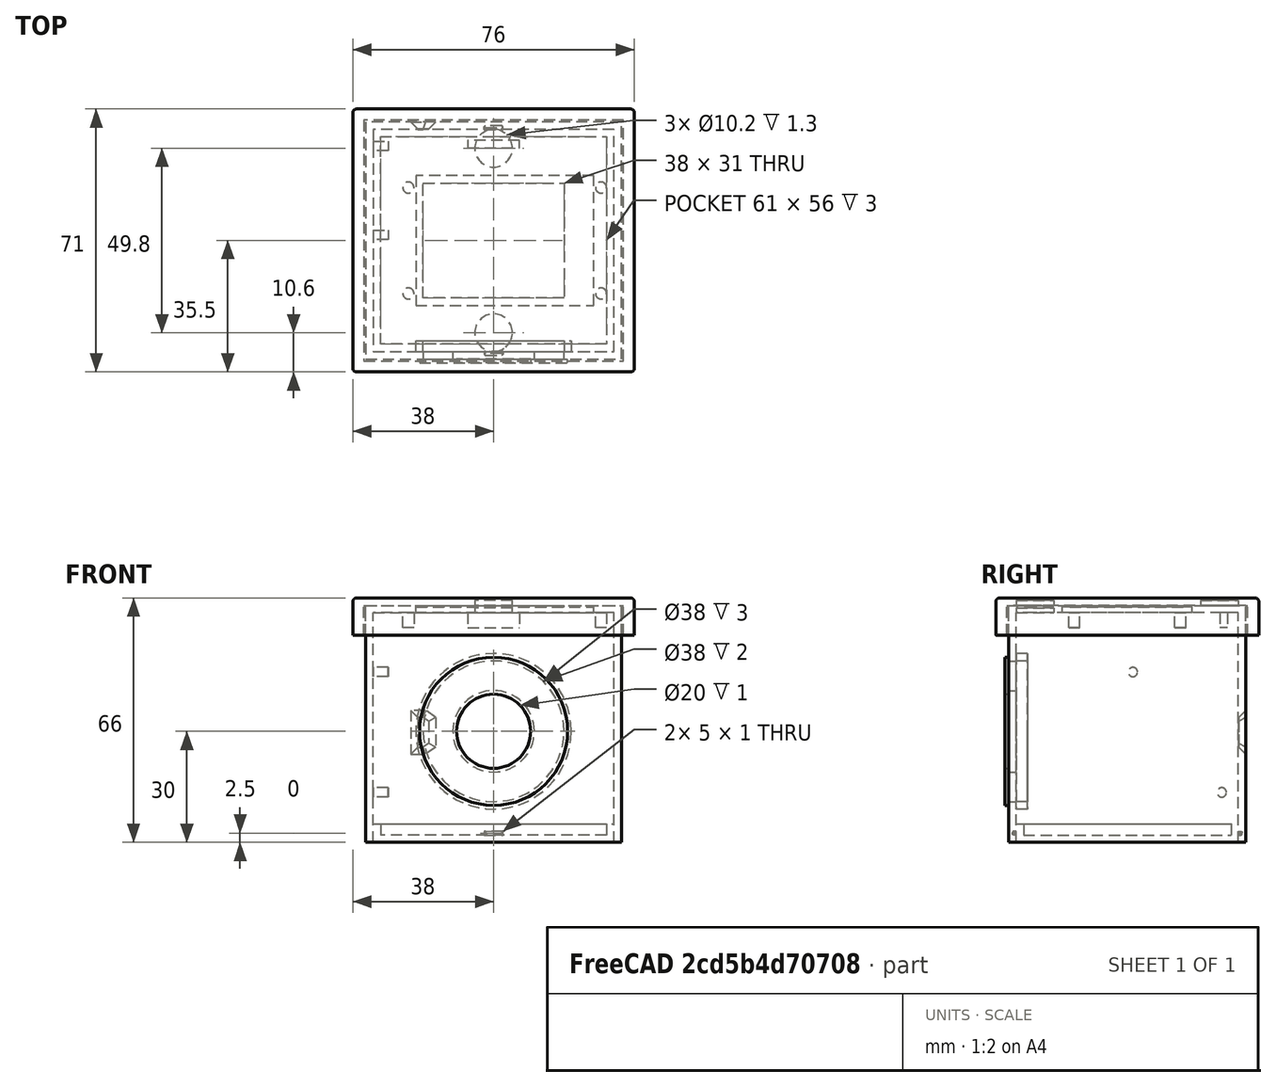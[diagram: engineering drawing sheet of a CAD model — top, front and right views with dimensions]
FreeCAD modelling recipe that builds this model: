
FCSTD DOCUMENT  (FreeCAD 0.18R16146 (Git))
Label: MessageBox
License: All rights reserved
LicenseURL: http://en.wikipedia.org/wiki/All_rights_reserved
objects: Sketcher::SketchObject×24, Part::Extrusion×24, PartDesign::ShapeBinder×17, Part::Cut×13, Part::MultiFuse×8, TechDraw::DrawViewDimension×5, TechDraw::DrawProjGroupItem×4, Part::Fillet×3, PartDesign::Body×3, TechDraw::DrawSVGTemplate×3, TechDraw::DrawPage×3, TechDraw::DrawViewSection×2, TechDraw::DrawProjGroup×2, PartDesign::Line×1, PartDesign::Plane×1, Part::Chamfer×1, Drawing::FeaturePage×1, TechDraw::DrawViewPart×1
note: 95 computed .brp shape members not serialized (recipe doc carries the construction recipe); baked Part::Feature solids carry a one-line shape summary decoded from their .brp

FEATURE [Sketcher::SketchObject] Sketch  label="Box Outline"
  MapMode = 5
  Support = -> [XY_Plane]
  sketch-geometry (6):
    g0: LineSegment StartX=-34.5 StartY=-32 StartZ=0 EndX=34.5 EndY=-32 EndZ=0
    g1: LineSegment StartX=34.5 StartY=-32 StartZ=0 EndX=34.5 EndY=32 EndZ=0
    g2: LineSegment StartX=34.5 StartY=32 StartZ=0 EndX=-34.5 EndY=32 EndZ=0
    g3: LineSegment StartX=-34.5 StartY=32 StartZ=0 EndX=-34.5 EndY=-32 EndZ=0
    g4: LineSegment [constr] StartX=-34.5 StartY=32 StartZ=0 EndX=0 EndY=0 EndZ=0
    g5: LineSegment [constr] StartX=0 StartY=0 StartZ=0 EndX=34.5 EndY=-32 EndZ=0
  constraints (17):
    c: Coincident(g0,g1)
    c: Coincident(g1,g2)
    c: Coincident(g2,g3)
    c: Coincident(g3,g0)
    c: Horizontal(g0)
    c: Horizontal(g2)
    c: Vertical(g1)
    c: Vertical(g3)
    c: DistanceX(g2,g2) = 69
    c: DistanceY(g1,g1) = 64
    c: Equal(g4,g5)
    c: Coincident(g5,g0)
    c: Coincident(g4,g-1)
    c: Coincident(g5,g-1)
    c: Equal(g5,g4)
    c: Coincident(g4,g2)
    c: Parallel(g5,g4)
FEATURE [Part::Extrusion] Extrude  label="Box Exterior Extrude"
  Base = -> Sketch
  Dir = (0,0,1)
  DirMode = 2
  FaceMakerClass = Part::FaceMakerBullseye
  LengthFwd = 64
  LengthRev = 0
  Solid = true
  Symmetric = false
FEATURE [PartDesign::ShapeBinder] CopyExtrude  label="Box Extrude"
  TraceSupport = false
FEATURE [Sketcher::SketchObject] Sketch001  label="Box Interior"
  ExternalGeometry = -> [Sketch]
  MapMode = 5
  Placement = pos=(0,0,0) rot=(1,0,0;3.14159rad)
  Support = -> [Extrude]
  sketch-geometry (4):
    g0: LineSegment StartX=32.5 StartY=-30 StartZ=0 EndX=-32.5 EndY=-30 EndZ=0
    g1: LineSegment StartX=-32.5 StartY=-30 StartZ=0 EndX=-32.5 EndY=30 EndZ=0
    g2: LineSegment StartX=-32.5 StartY=30 StartZ=0 EndX=32.5 EndY=30 EndZ=0
    g3: LineSegment StartX=32.5 StartY=30 StartZ=0 EndX=32.5 EndY=-30 EndZ=0
  constraints (12):
    c: Coincident(g0,g1)
    c: Coincident(g1,g2)
    c: Coincident(g2,g3)
    c: Coincident(g3,g0)
    c: Horizontal(g0)
    c: Horizontal(g2)
    c: Vertical(g1)
    c: Vertical(g3)
    c: DistanceY(g1,g-4) = 2
    c: DistanceY(g-6,g0) = 2
    c: DistanceX(g-4,g1) = 2
    c: DistanceX(g0,g-6) = 2
FEATURE [Part::Extrusion] Extrude001  label="Box Interior Extrude"
  Base = -> Sketch001
  Dir = (0,0,-1)
  DirMode = 2
  FaceMakerClass = Part::FaceMakerBullseye
  LengthFwd = 62
  LengthRev = 0
  Reversed = true
  Solid = true
  Symmetric = false
FEATURE [Part::Cut] Cut  label="Box Interior Cut"
  Base = -> Extrude
  Tool = -> Extrude001
FEATURE [PartDesign::ShapeBinder] CopyCut001  label="LCD Window Face"
  TraceSupport = false
FEATURE [PartDesign::ShapeBinder] CopyCut003
  TraceSupport = false
FEATURE [PartDesign::ShapeBinder] CopyCut003001
  TraceSupport = false
FEATURE [PartDesign::Line] DatumLine
  AttacherType = Attacher::AttachEngineLine
  MapMode = 29
  Placement = pos=(-0.000218501,-11.4897,2) rot=(-0.577343,0.577354,0.577354;4.18878rad)
  Support = -> [CopyCut003,CopyCut003001]
FEATURE [PartDesign::ShapeBinder] CopyCut003002
  TraceSupport = false
FEATURE [PartDesign::ShapeBinder] CopyCut003003
  TraceSupport = false
FEATURE [PartDesign::Plane] DatumPlane
  Length = 24
  MapMode = 13
  Placement = pos=(-1.67728,2.73005,1.33333) rot=(0.57735,0.57735,0.57735;2.0944rad)
  ResizeMode = 0
  Support = -> [CopyCut003002,CopyCut003003]
  Width = 24
FEATURE [PartDesign::ShapeBinder] ShapeBinder008  label="Body Interior Top"
  Placement = pos=(0,0,62) rot=(0,0,1;0rad)
  Support = -> [Cut]
  TraceSupport = false
FEATURE [Sketcher::SketchObject] Sketch002  label="LCD Window"
  ExternalGeometry = -> [ShapeBinder008]
  MapMode = 5
  Placement = pos=(0,0,62) rot=(1,0,0;3.14159rad)
  Support = -> [ShapeBinder008]
  sketch-geometry (10):
    g0: LineSegment StartX=-19 StartY=-15.5 StartZ=0 EndX=19 EndY=-15.5 EndZ=0
    g1: LineSegment StartX=19 StartY=-15.5 StartZ=0 EndX=19 EndY=15.5 EndZ=0
    g2: LineSegment StartX=19 StartY=15.5 StartZ=0 EndX=-19 EndY=15.5 EndZ=0
    g3: LineSegment [constr] StartX=19 StartY=15.5 StartZ=0 EndX=32.5 EndY=15.5 EndZ=0
    g4: LineSegment [constr] StartX=-19 StartY=15.5 StartZ=0 EndX=-32.5 EndY=15.5 EndZ=0
    g5: LineSegment [constr] StartX=-32.5 StartY=-30 StartZ=0 EndX=-32.5 EndY=7.1e-15 EndZ=0
    g6: LineSegment [constr] StartX=-32.5 StartY=5.3e-15 StartZ=0 EndX=-32.5 EndY=30 EndZ=0
    g7: LineSegment [constr] StartX=-19 StartY=15.5 StartZ=0 EndX=0 EndY=5.3e-15 EndZ=0
    g8: LineSegment [constr] StartX=0 StartY=5.3e-15 StartZ=0 EndX=19 EndY=-15.5 EndZ=0
    g9: LineSegment StartX=-19 StartY=15.5 StartZ=0 EndX=-19 EndY=-15.5 EndZ=0
  constraints (28):
    c: Coincident(g0,g1)
    c: Coincident(g1,g2)
    c: Horizontal(g0)
    c: Horizontal(g2)
    c: Vertical(g1)
    c: DistanceX(g2,g2) = 38
    c: DistanceY(g0,g2) = 31
    c: Horizontal(g3)
    c: Horizontal(g4)
    c: Equal(g3,g4)
    c: Coincident(g1,g3)
    c: Coincident(g2,g4)
    c: PointOnObject(g3,g-5)
    c: PointOnObject(g4,g-3)
    c: Equal(g5,g6)
    c: Coincident(g6,g5)
    c: Coincident(g5,g-6)
    c: Coincident(g-4,g6)
    c: Parallel(g5,g6)
    c: Coincident(g9,g2)
    c: Coincident(g9,g0)
    c: Vertical(g9)
    c: Equal(g7,g8)
    c: Coincident(g7,g2)
    c: Coincident(g7,g8)
    c: Coincident(g8,g0)
    c: Parallel(g7,g8)
    c: Horizontal(g7,g5)
FEATURE [Part::Extrusion] Extrude002  label="LCD Window Extrude"
  Base = -> Sketch002
  Dir = (0,0,-1)
  DirMode = 2
  FaceMakerClass = Part::FaceMakerBullseye
  LengthFwd = 2
  LengthRev = 0
  Reversed = true
  Solid = true
  Symmetric = false
FEATURE [Part::Cut] Cut001  label="LCD Window Cut"
  Base = -> Cut
  Tool = -> Extrude002
FEATURE [Sketcher::SketchObject] Sketch003  label="LCD Cutout"
  ExternalGeometry = -> [CopyCut001,Sketch002,ShapeBinder008]
  MapMode = 5
  Placement = pos=(0,0,62) rot=(1,0,0;3.14159rad)
  Support = -> [ShapeBinder008]
  sketch-geometry (4):
    g0: LineSegment StartX=-21 StartY=17.5 StartZ=0 EndX=27 EndY=17.5 EndZ=0
    g1: LineSegment StartX=27 StartY=17.5 StartZ=0 EndX=27 EndY=-17.5 EndZ=0
    g2: LineSegment StartX=27 StartY=-17.5 StartZ=0 EndX=-21 EndY=-17.5 EndZ=0
    g3: LineSegment StartX=-21 StartY=-17.5 StartZ=0 EndX=-21 EndY=17.5 EndZ=0
  constraints (12):
    c: Coincident(g0,g1)
    c: Coincident(g1,g2)
    c: Coincident(g2,g3)
    c: Coincident(g3,g0)
    c: Horizontal(g0)
    c: Horizontal(g2)
    c: Vertical(g1)
    c: Vertical(g3)
    c: DistanceY(g-5,g0) = 2
    c: DistanceY(g1,g-7) = 2
    c: DistanceX(g-7,g1) = 8
    c: DistanceX(g0,g-5) = 2
FEATURE [Part::Extrusion] Extrude003  label="LCD Cutout Extrude"
  Base = -> Sketch003
  Dir = (0,0,-1)
  DirMode = 2
  FaceMakerClass = Part::FaceMakerBullseye
  LengthFwd = 1.5
  LengthRev = 0
  Reversed = true
  Solid = true
  Symmetric = false
FEATURE [Part::Cut] Cut002  label="LCD Cutout Cut"
  Base = -> Cut001
  Tool = -> Extrude003
FEATURE [Sketcher::SketchObject] Sketch004  label="LCD Mounts"
  ExternalGeometry = -> [Sketch003]
  MapMode = 5
  Placement = pos=(0,0,62) rot=(1,0,0;3.14159rad)
  Support = -> [ShapeBinder008]
  sketch-geometry (12):
    g0: Circle CenterX=29 CenterY=14.3 CenterZ=0 NormalX=0 NormalY=0 NormalZ=1 AngleXU=0 Radius=1.5
    g1: Circle CenterX=-23 CenterY=14.3 CenterZ=0 NormalX=0 NormalY=0 NormalZ=1 AngleXU=0 Radius=1.5
    g2: Circle CenterX=-23 CenterY=-14.3 CenterZ=0 NormalX=0 NormalY=0 NormalZ=1 AngleXU=0 Radius=1.5
    g3: Circle CenterX=29 CenterY=-14.3 CenterZ=0 NormalX=0 NormalY=0 NormalZ=1 AngleXU=0 Radius=1.5
    g4: LineSegment [constr] StartX=27 StartY=17.5 StartZ=0 EndX=29 EndY=17.5 EndZ=0
    g5: LineSegment [constr] StartX=27 StartY=-17.5 StartZ=0 EndX=29 EndY=-17.5 EndZ=0
    g6: LineSegment [constr] StartX=-21 StartY=-17.5 StartZ=0 EndX=-23 EndY=-17.5 EndZ=0
    g7: LineSegment [constr] StartX=-21 StartY=17.5 StartZ=0 EndX=-23 EndY=17.5 EndZ=0
    g8: LineSegment [constr] StartX=-23 StartY=17.5 StartZ=0 EndX=-23 EndY=14.3 EndZ=0
    g9: LineSegment [constr] StartX=-23 StartY=-14.3 StartZ=0 EndX=-23 EndY=-17.5 EndZ=0
    g10: LineSegment [constr] StartX=29 StartY=17.5 StartZ=0 EndX=29 EndY=14.3 EndZ=0
    g11: LineSegment [constr] StartX=29 StartY=-14.3 StartZ=0 EndX=29 EndY=-17.5 EndZ=0
  constraints (32):
    c: Radius(g1) = 1.5
    c: Horizontal(g7)
    c: Horizontal(g4)
    c: Horizontal(g6)
    c: Horizontal(g5)
    c: Coincident(g-4,g7)
    c: Coincident(g-5,g4)
    c: Coincident(g5,g-6)
    c: Coincident(g6,g-6)
    c: Vertical(g2,g6)
    c: Vertical(g0,g4)
    c: Vertical(g3,g5)
    c: Equal(g1,g2)
    c: Equal(g3,g1)
    c: Equal(g1,g0)
    c: Equal(g5,g4)
    c: Equal(g4,g7)
    c: Equal(g7,g6)
    c: DistanceX(g7,g7) = 2
    c: Coincident(g7,g8)
    c: Coincident(g8,g1)
    c: Vertical(g8)
    c: DistanceY(g8,g8) = 3.2
    c: Coincident(g6,g9)
    c: Coincident(g2,g9)
    c: Coincident(g4,g10)
    c: Coincident(g0,g10)
    c: Coincident(g5,g11)
    c: Coincident(g3,g11)
    c: Equal(g11,g9)
    c: Equal(g9,g10)
    c: Equal(g10,g8)
FEATURE [Part::Extrusion] Extrude004  label="LCD Mount Extrusion"
  Base = -> Sketch004
  Dir = (0,0,-1)
  DirMode = 2
  FaceMakerClass = Part::FaceMakerBullseye
  LengthFwd = 4
  LengthRev = 0
  Solid = true
  Symmetric = false
FEATURE [Sketcher::SketchObject] Sketch005002  label="Symbol Exterior Outer"
  AttachmentOffset = pos=(0,0,0) rot=(0,0,1;3.14159rad)
  ExternalGeometry = -> [Cut002]
  MapMode = 5
  Placement = pos=(0,-32,0) rot=(0,-0.707107,0.707107;3.14159rad)
  Support = -> [Cut002]
  sketch-geometry (1):
    g0: Circle CenterX=0 CenterY=-30 CenterZ=0 NormalX=0 NormalY=0 NormalZ=1 AngleXU=0 Radius=20
  constraints (3):
    c: Diameter(g0) = 40
    c: DistanceY(g0,g-1) = 30
    c: PointOnObject(g0,g-2)
FEATURE [Part::Extrusion] Extrude005  label="Symbol Exterior Outer Extrude"
  Base = -> Sketch005002
  Dir = (0,-1,2e-16)
  DirMode = 2
  FaceMakerClass = Part::FaceMakerBullseye
  LengthFwd = 1
  LengthRev = 0
  Solid = true
  Symmetric = false
FEATURE [PartDesign::ShapeBinder] ShapeBinder  label="Box Interior Symbol Wall"
  Support = -> [Cut002]
  TraceSupport = false
FEATURE [Sketcher::SketchObject] Sketch005004  label="Symbol Interior Outer"
  MapMode = 5
  Placement = pos=(0,-30,0) rot=(0,0.707107,0.707107;3.14159rad)
  Support = -> [ShapeBinder]
  sketch-geometry (1):
    g0: Circle CenterX=0 CenterY=30 CenterZ=0 NormalX=0 NormalY=0 NormalZ=1 AngleXU=0 Radius=19
  constraints (3):
    c: Diameter(g0) = 38
    c: PointOnObject(g0,g-2)
    c: DistanceY(g-1,g0) = 30
FEATURE [Part::Extrusion] Extrude006  label="Symbol Interior Outer Extrude"
  Base = -> Sketch005004
  Dir = (0,1,-2e-16)
  DirMode = 2
  FaceMakerClass = Part::FaceMakerBullseye
  LengthFwd = 2
  LengthRev = 0
  Reversed = true
  Solid = true
  Symmetric = false
FEATURE [Sketcher::SketchObject] Sketch005017  label="Body Magnet Slot"
  ExternalGeometry = -> [ShapeBinder008]
  MapMode = 5
  Placement = pos=(0,0,62) rot=(1,0,0;3.14159rad)
  Support = -> [ShapeBinder008]
  sketch-geometry (3):
    g0: Circle CenterX=0 CenterY=24.9 CenterZ=0 NormalX=0 NormalY=0 NormalZ=1 AngleXU=0 Radius=5.1
    g1: LineSegment [constr] StartX=-32.5 StartY=30 StartZ=0 EndX=0 EndY=30 EndZ=0
    g2: LineSegment [constr] StartX=0 StartY=30 StartZ=0 EndX=32.5 EndY=30 EndZ=0
  constraints (8):
    c: Radius(g0) = 5.1
    c: Coincident(g2,g1)
    c: Equal(g1,g2)
    c: PointOnObject(g1,g0)
    c: Vertical(g0,g1)
    c: Coincident(g1,g-3)
    c: Coincident(g-3,g2)
    c: PointOnObject(g1,g-3)
FEATURE [Part::Extrusion] Extrude018  label="Body Magnet Slot Extrude"
  Base = -> Sketch005017
  Dir = (0,0,-1)
  DirMode = 2
  FaceMakerClass = Part::FaceMakerBullseye
  LengthFwd = 1.3
  LengthRev = 0
  Reversed = true
  Solid = true
  Symmetric = false
FEATURE [Sketcher::SketchObject] Sketch005018  label="Lid Exterior"
  MapMode = 5
  Support = -> [XY_Plane001]
  sketch-geometry (6):
    g0: LineSegment StartX=-38 StartY=35.5 StartZ=0 EndX=38 EndY=35.5 EndZ=0
    g1: LineSegment StartX=38 StartY=35.5 StartZ=0 EndX=38 EndY=-35.5 EndZ=0
    g2: LineSegment StartX=38 StartY=-35.5 StartZ=0 EndX=-38 EndY=-35.5 EndZ=0
    g3: LineSegment StartX=-38 StartY=-35.5 StartZ=0 EndX=-38 EndY=35.5 EndZ=0
    g4: LineSegment [constr] StartX=38 StartY=35.5 StartZ=0 EndX=0 EndY=0 EndZ=0
    g5: LineSegment [constr] StartX=0 StartY=0 StartZ=0 EndX=-38 EndY=-35.5 EndZ=0
  constraints (16):
    c: Coincident(g0,g1)
    c: Coincident(g1,g2)
    c: Coincident(g2,g3)
    c: Coincident(g3,g0)
    c: Horizontal(g0)
    c: Horizontal(g2)
    c: Vertical(g1)
    c: Vertical(g3)
    c: DistanceX(g0,g0) = 76
    c: DistanceY(g3,g3) = 71
    c: Coincident(g4,g0)
    c: Coincident(g5,g4)
    c: Coincident(g5,g2)
    c: Parallel(g4,g5)
    c: Coincident(g4,g-1)
    c: Equal(g5,g4)
FEATURE [Part::Extrusion] Extrude015  label="Lid Exterior Extrude"
  Base = -> Sketch005018
  Dir = (0,0,1)
  DirMode = 2
  FaceMakerClass = Part::FaceMakerBullseye
  LengthFwd = 10
  LengthRev = 0
  Solid = true
  Symmetric = false
FEATURE [PartDesign::ShapeBinder] ShapeBinder012
  Support = -> [Extrude015]
  TraceSupport = false
FEATURE [PartDesign::ShapeBinder] CopyExtrude015
  TraceSupport = false
FEATURE [Sketcher::SketchObject] Sketch005019  label="Lid Interior"
  ExternalGeometry = -> [Sketch005018]
  MapMode = 5
  Placement = pos=(0,0,0) rot=(1,0,0;3.14159rad)
  Support = -> [CopyExtrude015]
  sketch-geometry (4):
    g0: LineSegment StartX=-35 StartY=32.5 StartZ=0 EndX=35 EndY=32.5 EndZ=0
    g1: LineSegment StartX=35 StartY=32.5 StartZ=0 EndX=35 EndY=-32.5 EndZ=0
    g2: LineSegment StartX=35 StartY=-32.5 StartZ=0 EndX=-35 EndY=-32.5 EndZ=0
    g3: LineSegment StartX=-35 StartY=-32.5 StartZ=0 EndX=-35 EndY=32.5 EndZ=0
  constraints (12):
    c: Coincident(g0,g1)
    c: Coincident(g1,g2)
    c: Coincident(g2,g3)
    c: Coincident(g3,g0)
    c: Horizontal(g0)
    c: Horizontal(g2)
    c: Vertical(g1)
    c: Vertical(g3)
    c: DistanceY(g0,g-4) = 3
    c: DistanceY(g-6,g1) = 3
    c: DistanceX(g-4,g0) = 3
    c: DistanceX(g1,g-6) = 3
FEATURE [Part::Extrusion] Extrude016  label="Lid Interior Extrude"
  Base = -> Sketch005019
  Dir = (0,0,-1)
  DirMode = 2
  FaceMakerClass = Part::FaceMakerBullseye
  LengthFwd = 8
  LengthRev = 0
  Reversed = true
  Solid = true
  Symmetric = false
FEATURE [Part::Cut] Cut008  label="Lid Interior Cut"
  Base = -> Extrude015
  Placement = pos=(0,0,56) rot=(0,0,1;0rad)
  Tool = -> Extrude016
FEATURE [Part::Fillet] Fillet  label="Lid Edge Fillet"
  Base = -> Cut008
  Edges = 8 edges r=1: [Edge1,Edge2,Edge4,Edge5,Edge7,Edge8,Edge10,Edge16]
FEATURE [PartDesign::ShapeBinder] ShapeBinder013  label="LidInterior"
  Placement = pos=(0,0,64) rot=(0,0,1;0rad)
  Support = -> [Cut008]
  TraceSupport = false
FEATURE [Sketcher::SketchObject] Sketch005020  label="Lid Magnet Slots"
  ExternalGeometry = -> [ShapeBinder013]
  MapMode = 5
  Placement = pos=(0,0,64) rot=(1,0,0;3.14159rad)
  Support = -> [ShapeBinder013]
  sketch-geometry (7):
    g0: Circle CenterX=8e-16 CenterY=24.9 CenterZ=0 NormalX=0 NormalY=0 NormalZ=1 AngleXU=0 Radius=5.1
    g1: Circle CenterX=8e-16 CenterY=-24.9 CenterZ=0 NormalX=0 NormalY=0 NormalZ=1 AngleXU=0 Radius=5.1
    g2: LineSegment [constr] StartX=-35 StartY=32.5 StartZ=0 EndX=0 EndY=32.5 EndZ=0
    g3: LineSegment [constr] StartX=8e-16 StartY=32.5 StartZ=0 EndX=35 EndY=32.5 EndZ=0
    g4: LineSegment [constr] StartX=8e-16 StartY=32.5 StartZ=0 EndX=8e-16 EndY=-32.5 EndZ=0
    g5: GeomPoint X=8e-16 Y=30 Z=0
    g6: GeomPoint X=8e-16 Y=-30 Z=0
  constraints (18):
    c: Equal(g1,g0)
    c: Diameter(g0) = 10.2
    c: PointOnObject(g2,g-4)
    c: PointOnObject(g1,g4)
    c: PointOnObject(g0,g4)
    c: PointOnObject(g5,g4)
    c: PointOnObject(g5,g0)
    c: PointOnObject(g6,g4)
    c: PointOnObject(g6,g1)
    c: DistanceY(g4,g6) = 2.5
    c: DistanceY(g5,g2) = 2.5
    c: Coincident(g3,g-4)
    c: Coincident(g2,g-4)
    c: Coincident(g2,g3)
    c: Coincident(g4,g2)
    c: Equal(g3,g2)
    c: PointOnObject(g4,g-5)
    c: Vertical(g4)
FEATURE [Part::Extrusion] Extrude017  label="Lid Magnet Slot Extrusion"
  Base = -> Sketch005020
  Dir = (0,0,-1)
  DirMode = 2
  FaceMakerClass = Part::FaceMakerBullseye
  LengthFwd = 1.3
  LengthRev = 0
  Reversed = true
  Solid = true
  Symmetric = false
FEATURE [Part::Cut] Cut009  label="Lid Magnet Slot Cut"
  Base = -> Fillet
  Tool = -> Extrude017
FEATURE [PartDesign::Body] Body001  label="Lid"
  Group = -> [Sketch005018,ShapeBinder012,CopyExtrude015,Sketch005019,ShapeBinder013,Sketch005020]
  Origin = -> Origin001
FEATURE [Sketcher::SketchObject] Sketch005021  label="Bottom Base"
  MapMode = 5
  Support = -> [XY_Plane002]
  sketch-geometry (6):
    g0: LineSegment StartX=-32.5 StartY=30 StartZ=0 EndX=32.5 EndY=30 EndZ=0
    g1: LineSegment StartX=32.5 StartY=30 StartZ=0 EndX=32.5 EndY=-30 EndZ=0
    g2: LineSegment StartX=32.5 StartY=-30 StartZ=0 EndX=-32.5 EndY=-30 EndZ=0
    g3: LineSegment StartX=-32.5 StartY=-30 StartZ=0 EndX=-32.5 EndY=30 EndZ=0
    g4: LineSegment [constr] StartX=-32.5 StartY=30 StartZ=0 EndX=0 EndY=0 EndZ=0
    g5: LineSegment [constr] StartX=0 StartY=0 StartZ=0 EndX=32.5 EndY=-30 EndZ=0
  constraints (16):
    c: Coincident(g0,g1)
    c: Coincident(g1,g2)
    c: Coincident(g2,g3)
    c: Coincident(g3,g0)
    c: Horizontal(g0)
    c: Horizontal(g2)
    c: Vertical(g1)
    c: Vertical(g3)
    c: DistanceX(g0,g0) = 65
    c: DistanceY(g1,g1) = 60
    c: Coincident(g4,g0)
    c: Coincident(g4,g-1)
    c: Coincident(g5,g-1)
    c: Coincident(g5,g1)
    c: Equal(g4,g5)
    c: Parallel(g4,g5)
FEATURE [Part::Extrusion] Extrude019  label="Bottom Base Extrusion"
  Base = -> Sketch005021
  Dir = (0,0,1)
  DirMode = 2
  FaceMakerClass = Part::FaceMakerBullseye
  LengthFwd = 5
  LengthRev = 0
  Solid = true
  Symmetric = false
FEATURE [PartDesign::ShapeBinder] ShapeBinder014  label="Bottom Base Top"
  Placement = pos=(0,0,5) rot=(0,0,1;0rad)
  Support = -> [Extrude019]
  TraceSupport = false
FEATURE [Sketcher::SketchObject] Sketch005022  label="Bottom Base Interior"
  ExternalGeometry = -> [ShapeBinder014]
  MapMode = 5
  Placement = pos=(0,0,5) rot=(0,0,1;0rad)
  Support = -> [ShapeBinder014]
  sketch-geometry (4):
    g0: LineSegment StartX=-30.5 StartY=28 StartZ=0 EndX=30.5 EndY=28 EndZ=0
    g1: LineSegment StartX=30.5 StartY=28 StartZ=0 EndX=30.5 EndY=-28 EndZ=0
    g2: LineSegment StartX=30.5 StartY=-28 StartZ=0 EndX=-30.5 EndY=-28 EndZ=0
    g3: LineSegment StartX=-30.5 StartY=-28 StartZ=0 EndX=-30.5 EndY=28 EndZ=0
  constraints (12):
    c: Coincident(g0,g1)
    c: Coincident(g1,g2)
    c: Coincident(g2,g3)
    c: Coincident(g3,g0)
    c: Horizontal(g0)
    c: Horizontal(g2)
    c: Vertical(g1)
    c: Vertical(g3)
    c: DistanceY(g0,g-6) = 2
    c: DistanceY(g-5,g1) = 2
    c: DistanceX(g-6,g0) = 2
    c: DistanceX(g1,g-5) = 2
FEATURE [Part::Extrusion] Extrude020  label="Bottom Base Interior Extrusion"
  Base = -> Sketch005022
  Dir = (0,0,1)
  DirMode = 2
  FaceMakerClass = Part::FaceMakerBullseye
  LengthFwd = 3
  LengthRev = 0
  Reversed = true
  Solid = true
  Symmetric = false
FEATURE [Part::Cut] Cut011  label="Bottom Base Interior Cut"
  Base = -> Extrude019
  Tool = -> Extrude020
FEATURE [PartDesign::ShapeBinder] ShapeBinder015  label="Bottom Base Front"
  Support = -> [Cut011]
  TraceSupport = false
FEATURE [PartDesign::ShapeBinder] ShapeBinder016  label="Bottom Base Rear"
  Support = -> [Cut011]
  TraceSupport = false
FEATURE [Sketcher::SketchObject] Sketch005023  label="Bottom Tab Front"
  ExternalGeometry = -> [ShapeBinder014,ShapeBinder015]
  MapMode = 5
  Placement = pos=(0,-30,0) rot=(1,0,0;1.5708rad)
  Support = -> [ShapeBinder015]
  sketch-geometry (6):
    g0: LineSegment StartX=-2.5 StartY=3 StartZ=0 EndX=2.5 EndY=3 EndZ=0
    g1: LineSegment StartX=2.5 StartY=3 StartZ=0 EndX=2.5 EndY=2 EndZ=0
    g2: LineSegment StartX=2.5 StartY=2 StartZ=0 EndX=-2.5 EndY=2 EndZ=0
    g3: LineSegment StartX=-2.5 StartY=2 StartZ=0 EndX=-2.5 EndY=3 EndZ=0
    g4: LineSegment [constr] StartX=-2.5 StartY=3 StartZ=0 EndX=0 EndY=2.5 EndZ=0
    g5: LineSegment [constr] StartX=0 StartY=2.5 StartZ=0 EndX=2.5 EndY=2 EndZ=0
  constraints (17):
    c: Coincident(g0,g1)
    c: Coincident(g1,g2)
    c: Coincident(g2,g3)
    c: Coincident(g3,g0)
    c: Horizontal(g0)
    c: Horizontal(g2)
    c: Vertical(g1)
    c: Vertical(g3)
    c: DistanceX(g0,g0) = 5
    c: DistanceY(g1,g1) = 1
    c: DistanceY(g-4,g1) = 2
    c: Coincident(g4,g0)
    c: PointOnObject(g4,g-2)
    c: Coincident(g5,g4)
    c: Coincident(g5,g1)
    c: Equal(g4,g5)
    c: Parallel(g4,g5)
FEATURE [Part::Extrusion] Extrude021  label="Bottom Tab Front Extrusion"
  Base = -> Sketch005023
  Dir = (0,-1,2e-16)
  DirMode = 2
  FaceMakerClass = Part::FaceMakerBullseye
  LengthFwd = 0.5
  LengthRev = 0
  Solid = true
  Symmetric = false
FEATURE [Sketcher::SketchObject] Sketch005024  label="Bottom Tab Rear"
  ExternalGeometry = -> [ShapeBinder014,ShapeBinder016]
  MapMode = 5
  Placement = pos=(0,30,0) rot=(0,0.707107,0.707107;3.14159rad)
  Support = -> [ShapeBinder016]
  sketch-geometry (6):
    g0: LineSegment StartX=-2.5 StartY=3 StartZ=0 EndX=2.5 EndY=3 EndZ=0
    g1: LineSegment StartX=2.5 StartY=3 StartZ=0 EndX=2.5 EndY=2 EndZ=0
    g2: LineSegment StartX=2.5 StartY=2 StartZ=0 EndX=-2.5 EndY=2 EndZ=0
    g3: LineSegment StartX=-2.5 StartY=2 StartZ=0 EndX=-2.5 EndY=3 EndZ=0
    g4: LineSegment [constr] StartX=-2.5 StartY=3 StartZ=0 EndX=0 EndY=2.5 EndZ=0
    g5: LineSegment [constr] StartX=0 StartY=2.5 StartZ=0 EndX=2.5 EndY=2 EndZ=0
  constraints (17):
    c: Coincident(g0,g1)
    c: Coincident(g1,g2)
    c: Coincident(g2,g3)
    c: Coincident(g3,g0)
    c: Horizontal(g0)
    c: Horizontal(g2)
    c: Vertical(g1)
    c: Vertical(g3)
    c: Coincident(g4,g0)
    c: PointOnObject(g4,g-2)
    c: Coincident(g5,g4)
    c: Coincident(g5,g1)
    c: Parallel(g4,g5)
    c: Equal(g4,g5)
    c: DistanceX(g0,g0) = 5
    c: DistanceY(g1,g1) = 1
    c: DistanceY(g-4,g1) = 2
FEATURE [PartDesign::Body] Body002
  Group = -> [Sketch005021,ShapeBinder014,Sketch005022,ShapeBinder015,ShapeBinder016,Sketch005023,Sketch005024]
  Origin = -> Origin002
FEATURE [Part::Extrusion] Extrude022  label="Bottom Tab Rear Extrusion"
  Base = -> Sketch005024
  Dir = (0,1,-2e-16)
  DirMode = 2
  FaceMakerClass = Part::FaceMakerBullseye
  LengthFwd = 0.5
  LengthRev = 0
  Solid = true
  Symmetric = false
FEATURE [Part::MultiFuse] Fusion006  label="Bottom Tabs"
  Shapes = -> [Extrude022,Extrude021]
FEATURE [Part::Fillet] Fillet002  label="Bottom Base Tab Fillet"
  Base = -> Fusion006
  Edges = 8 edges r=0.4: [Edge4,Edge7,Edge10,Edge12,Edge16,Edge19,Edge22,Edge24]
FEATURE [Part::MultiFuse] Fusion007  label="Bottom Base Fusion"
  Shapes = -> [Fillet002,Cut011]
FEATURE [Sketcher::SketchObject] Sketch005026  label="Body Bottom Tab Front"
  ExternalGeometry = -> [ShapeBinder]
  MapMode = 5
  Placement = pos=(0,-30,0) rot=(0,0.707107,0.707107;3.14159rad)
  Support = -> [ShapeBinder]
  sketch-geometry (6):
    g0: LineSegment StartX=-2.5 StartY=3 StartZ=0 EndX=2.5 EndY=3 EndZ=0
    g1: LineSegment StartX=2.5 StartY=3 StartZ=0 EndX=2.5 EndY=2 EndZ=0
    g2: LineSegment StartX=2.5 StartY=2 StartZ=0 EndX=-2.5 EndY=2 EndZ=0
    g3: LineSegment StartX=-2.5 StartY=2 StartZ=0 EndX=-2.5 EndY=3 EndZ=0
    g4: LineSegment [constr] StartX=-2.5 StartY=3 StartZ=0 EndX=0 EndY=2.5 EndZ=0
    g5: LineSegment [constr] StartX=0 StartY=2.5 StartZ=0 EndX=2.5 EndY=2 EndZ=0
  constraints (17):
    c: Coincident(g0,g1)
    c: Coincident(g1,g2)
    c: Coincident(g2,g3)
    c: Coincident(g3,g0)
    c: Horizontal(g0)
    c: Horizontal(g2)
    c: Vertical(g1)
    c: Vertical(g3)
    c: Coincident(g4,g0)
    c: PointOnObject(g4,g-2)
    c: Coincident(g5,g4)
    c: Coincident(g5,g1)
    c: Equal(g4,g5)
    c: Parallel(g4,g5)
    c: DistanceX(g0,g0) = 5
    c: DistanceY(g1,g1) = 1
    c: DistanceY(g-3,g2) = 2
FEATURE [Part::Extrusion] Extrude024  label="Body Bottom Tab Front Extrusion"
  Base = -> Sketch005026
  Dir = (0,1,-2e-16)
  DirMode = 2
  FaceMakerClass = Part::FaceMakerBullseye
  LengthFwd = 1
  LengthRev = 0
  Reversed = true
  Solid = true
  Symmetric = false
FEATURE [PartDesign::ShapeBinder] CopyCut002
  TraceSupport = false
FEATURE [Sketcher::SketchObject] Sketch005027  label="Symbol Exterior Inner"
  MapMode = 5
  Placement = pos=(0,-32,0) rot=(1,0,0;1.5708rad)
  Support = -> [CopyCut002]
  sketch-geometry (1):
    g0: Circle CenterX=0 CenterY=30 CenterZ=0 NormalX=0 NormalY=0 NormalZ=1 AngleXU=0 Radius=10
  constraints (3):
    c: PointOnObject(g0,g-2)
    c: Diameter(g0) = 20
    c: DistanceY(g-1,g0) = 30
FEATURE [Part::Extrusion] Extrude025  label="Symbol Exterior Inner Extrude"
  Base = -> Sketch005027
  Dir = (0,-1,2e-16)
  DirMode = 2
  FaceMakerClass = Part::FaceMakerBullseye
  LengthFwd = 1
  LengthRev = 0
  Solid = true
  Symmetric = false
FEATURE [Part::Cut] Cut012  label="Symbol Exterior Ring Cut"
  Base = -> Extrude005
  Tool = -> Extrude025
FEATURE [Sketcher::SketchObject] Sketch005028  label="Symbol Interior Inner"
  MapMode = 5
  Placement = pos=(0,-30,0) rot=(0,0.707107,0.707107;3.14159rad)
  Support = -> [ShapeBinder]
  sketch-geometry (1):
    g0: Circle CenterX=0 CenterY=30 CenterZ=0 NormalX=0 NormalY=0 NormalZ=1 AngleXU=0 Radius=11
  constraints (3):
    c: PointOnObject(g0,g-2)
    c: Diameter(g0) = 22
    c: DistanceY(g-1,g0) = 30
FEATURE [Part::Extrusion] Extrude026  label="Symbol Interior Inner Extrude"
  Base = -> Sketch005028
  Dir = (0,1,-2e-16)
  DirMode = 2
  FaceMakerClass = Part::FaceMakerBullseye
  LengthFwd = 2
  LengthRev = 0
  Reversed = true
  Solid = true
  Symmetric = false
FEATURE [Part::Cut] Cut013  label="Symbol Interior Ring Cut"
  Base = -> Extrude006
  Tool = -> Extrude026
FEATURE [Part::Cut] Cut003  label="Symbol Interior Cut"
  Base = -> Cut002
  Tool = -> Cut013
FEATURE [PartDesign::ShapeBinder] ShapeBinder009  label="Body Interior Rear"
  Support = -> [Cut003]
  TraceSupport = false
FEATURE [Sketcher::SketchObject] Sketch005012  label="Micro-USB Cutout"
  ExternalGeometry = -> [ShapeBinder009]
  MapMode = 5
  Placement = pos=(0,30,0) rot=(1,0,0;1.5708rad)
  Support = -> [ShapeBinder009]
  sketch-geometry (11):
    g0: LineSegment [constr] StartX=-32.5 StartY=10 StartZ=0 EndX=-17.5 EndY=10 EndZ=0
    g1: LineSegment [constr] StartX=-17.5 StartY=49.5 StartZ=0 EndX=-32.5 EndY=49.5 EndZ=0
    g2: LineSegment [constr] StartX=-32.5 StartY=49.5 StartZ=0 EndX=-32.5 EndY=10 EndZ=0
    g3: LineSegment [constr] StartX=-17.5 StartY=49.5 StartZ=0 EndX=-17.5 EndY=32.75 EndZ=0
    g4: LineSegment StartX=-17.5 StartY=32.75 StartZ=0 EndX=-17.5 EndY=26.75 EndZ=0
    g5: LineSegment [constr] StartX=-17.5 StartY=26.75 StartZ=0 EndX=-17.5 EndY=10 EndZ=0
    g6: LineSegment StartX=-17.5 StartY=32.75 StartZ=0 EndX=-19 EndY=33.75 EndZ=0
    g7: LineSegment StartX=-17.5 StartY=26.75 StartZ=0 EndX=-19 EndY=25.75 EndZ=0
    g8: LineSegment StartX=-19 StartY=33.75 StartZ=0 EndX=-20.5 EndY=33.75 EndZ=0
    g9: LineSegment StartX=-20.5 StartY=33.75 StartZ=0 EndX=-20.5 EndY=25.75 EndZ=0
    g10: LineSegment StartX=-20.5 StartY=25.75 StartZ=0 EndX=-19 EndY=25.75 EndZ=0
  constraints (32):
    c: Coincident(g1,g2)
    c: Coincident(g2,g0)
    c: Horizontal(g0)
    c: Horizontal(g1)
    c: Vertical(g2)
    c: DistanceX(g0,g0) = 15
    c: DistanceY(g0,g1) = 39.5
    c: Coincident(g4,g3)
    c: Vertical(g4)
    c: Coincident(g5,g4)
    c: Coincident(g5,g0)
    c: DistanceY(g4,g4) = 6
    c: Equal(g3,g5)
    c: Vertical(g3)
    c: Vertical(g5)
    c: Coincident(g6,g4)
    c: Coincident(g7,g4)
    c: Coincident(g8,g6)
    c: Coincident(g9,g8)
    c: Coincident(g10,g9)
    c: Coincident(g10,g7)
    c: Equal(g8,g10)
    c: Coincident(g1,g3)
    c: DistanceY(g9,g9) = 8
    c: DistanceY(g-4,g0) = 10
    c: Vertical(g0,g-4)
    c: Vertical(g9)
    c: Perpendicular(g9,g10)
    c: DistanceX(g10,g10) = 1.5
    c: DistanceX(g9,g4) = 3
    c: Perpendicular(g9,g8)
    c: Equal(g6,g7)
FEATURE [Part::Extrusion] Extrude013  label="Micro-USB Cutout Extrusion"
  Base = -> Sketch005012
  Dir = (0,-1,2e-16)
  DirMode = 2
  FaceMakerClass = Part::FaceMakerBullseye
  LengthFwd = 2
  LengthRev = 0
  Reversed = true
  Solid = true
  Symmetric = false
FEATURE [Part::Cut] Cut007  label="Micro-USB Cut"
  Base = -> Cut003
  Tool = -> Extrude013
FEATURE [Sketcher::SketchObject] Sketch005013  label="Reed Mount"
  ExternalGeometry = -> [ShapeBinder009]
  MapMode = 5
  Placement = pos=(0,0,62) rot=(1,0,0;3.14159rad)
  Support = -> [ShapeBinder008]
  sketch-geometry (6):
    g0: LineSegment StartX=-7 StartY=-25 StartZ=0 EndX=7 EndY=-25 EndZ=0
    g1: LineSegment StartX=7 StartY=-25 StartZ=0 EndX=7 EndY=-27 EndZ=0
    g2: LineSegment StartX=7 StartY=-27 StartZ=0 EndX=-7 EndY=-27 EndZ=0
    g3: LineSegment StartX=-7 StartY=-27 StartZ=0 EndX=-7 EndY=-25 EndZ=0
    g4: LineSegment [constr] StartX=-32.5 StartY=-30 StartZ=0 EndX=-7 EndY=-25 EndZ=0
    g5: LineSegment [constr] StartX=32.5 StartY=-30 StartZ=0 EndX=7 EndY=-25 EndZ=0
  constraints (16):
    c: Coincident(g0,g1)
    c: Coincident(g1,g2)
    c: Coincident(g2,g3)
    c: Coincident(g3,g0)
    c: Horizontal(g0)
    c: Horizontal(g2)
    c: Vertical(g1)
    c: Vertical(g3)
    c: DistanceX(g2,g2) = 14
    c: DistanceY(g1,g1) = 2
    c: Coincident(g4,g-3)
    c: Coincident(g4,g0)
    c: Coincident(g5,g-3)
    c: Coincident(g5,g0)
    c: Equal(g5,g4)
    c: DistanceY(g5,g1) = 3
FEATURE [Part::Extrusion] Extrude014  label="Reed Mount Extrusion"
  Base = -> Sketch005013
  Dir = (0,0,-1)
  DirMode = 2
  FaceMakerClass = Part::FaceMakerBullseye
  LengthFwd = 4
  LengthRev = 0
  Solid = true
  Symmetric = false
FEATURE [PartDesign::ShapeBinder] ShapeBinder010
  Support = -> [Cut003]
  TraceSupport = false
FEATURE [Sketcher::SketchObject] Sketch005011  label="MCU Mounts"
  ExternalGeometry = -> [ShapeBinder010]
  MapMode = 5
  Placement = pos=(-32.5,0,0) rot=(0.57735,0.57735,0.57735;2.0944rad)
  Support = -> [ShapeBinder010]
  sketch-geometry (10):
    g0: LineSegment [constr] StartX=-2 StartY=49.5 StartZ=0 EndX=29 EndY=49.5 EndZ=0
    g1: LineSegment [constr] StartX=29 StartY=49.5 StartZ=0 EndX=29 EndY=10 EndZ=0
    g2: LineSegment [constr] StartX=29 StartY=10 StartZ=0 EndX=-2 EndY=10 EndZ=0
    g3: LineSegment [constr] StartX=-2 StartY=10 StartZ=0 EndX=-2 EndY=49.5 EndZ=0
    g4: Circle CenterX=25.5 CenterY=13.5 CenterZ=0 NormalX=0 NormalY=0 NormalZ=1 AngleXU=0 Radius=1.25
    g5: Circle CenterX=1.5 CenterY=46 CenterZ=0 NormalX=0 NormalY=0 NormalZ=1 AngleXU=0 Radius=1.25
    g6: LineSegment [constr] StartX=25.5 StartY=10 StartZ=0 EndX=25.5 EndY=13.5 EndZ=0
    g7: LineSegment [constr] StartX=25.5 StartY=13.5 StartZ=0 EndX=29 EndY=13.5 EndZ=0
    g8: LineSegment [constr] StartX=1.5 StartY=46 StartZ=0 EndX=-2 EndY=46 EndZ=0
    g9: LineSegment [constr] StartX=1.5 StartY=49.5 StartZ=0 EndX=1.5 EndY=46 EndZ=0
  constraints (30):
    c: Coincident(g1,g2)
    c: Coincident(g2,g3)
    c: Coincident(g3,g0)
    c: Horizontal(g0)
    c: Horizontal(g2)
    c: Vertical(g1)
    c: Vertical(g3)
    c: DistanceY(g1,g1) = 39.5
    c: Equal(g5,g4)
    c: Coincident(g6,g7)
    c: Horizontal(g7)
    c: Vertical(g6)
    c: Coincident(g6,g4)
    c: Coincident(g9,g8)
    c: Horizontal(g8)
    c: Vertical(g9)
    c: Coincident(g8,g5)
    c: Diameter(g4) = 2.5
    c: PointOnObject(g7,g1)
    c: PointOnObject(g8,g3)
    c: DistanceY(g-3,g1) = 10
    c: Equal(g9,g8)
    c: PointOnObject(g9,g0)
    c: Coincident(g0,g1)
    c: PointOnObject(g6,g2)
    c: DistanceY(g6,g6) = 3.5
    c: Equal(g7,g6)
    c: Equal(g9,g6)
    c: DistanceX(g0,g0) = 31
    c: DistanceX(g0,g-3) = 1
FEATURE [Part::Extrusion] Extrude012  label="MCU Mount Extrusion"
  Base = -> Sketch005011
  Dir = (1,0,0)
  DirMode = 2
  FaceMakerClass = Part::FaceMakerBullseye
  LengthFwd = 4
  LengthRev = 0
  Solid = true
  Symmetric = false
FEATURE [Part::Chamfer] Chamfer  label="Micro-USB Port Flare"
  Base = -> Cut007
  Edges = 6 edges r=1.9: [Edge24,Edge25,Edge26,Edge27,Edge28,Edge29]
FEATURE [Part::MultiFuse] Fusion001  label="MCU Mount Fusion"
  Shapes = -> [Extrude012,Chamfer]
FEATURE [Part::MultiFuse] Fusion002  label="Exterior Symbol Fusion"
  Shapes = -> [Fusion001,Cut012]
FEATURE [Part::Cut] Cut010  label="Body Magnet Slot Cut"
  Base = -> Fusion002
  Tool = -> Extrude018
FEATURE [Part::MultiFuse] Fusion003  label="Reed Mount Fusion"
  Shapes = -> [Cut010,Extrude014]
FEATURE [Part::MultiFuse] Fusion004  label="LCD Mount Fusion"
  Shapes = -> [Extrude004,Fusion003]
FEATURE [Sketcher::SketchObject] Sketch005025  label="Body Bottom Tab Rear"
  ExternalGeometry = -> [ShapeBinder009]
  MapMode = 5
  Placement = pos=(0,30,0) rot=(1,0,0;1.5708rad)
  Support = -> [ShapeBinder009]
  sketch-geometry (6):
    g0: LineSegment StartX=-2.5 StartY=3 StartZ=0 EndX=2.5 EndY=3 EndZ=0
    g1: LineSegment StartX=2.5 StartY=3 StartZ=0 EndX=2.5 EndY=2 EndZ=0
    g2: LineSegment StartX=2.5 StartY=2 StartZ=0 EndX=-2.5 EndY=2 EndZ=0
    g3: LineSegment StartX=-2.5 StartY=2 StartZ=0 EndX=-2.5 EndY=3 EndZ=0
    g4: LineSegment [constr] StartX=-2.5 StartY=3 StartZ=0 EndX=0 EndY=2.5 EndZ=0
    g5: LineSegment [constr] StartX=0 StartY=2.5 StartZ=0 EndX=2.5 EndY=2 EndZ=0
  constraints (17):
    c: Coincident(g0,g1)
    c: Coincident(g1,g2)
    c: Coincident(g2,g3)
    c: Coincident(g3,g0)
    c: Horizontal(g0)
    c: Horizontal(g2)
    c: Vertical(g1)
    c: Vertical(g3)
    c: Coincident(g4,g0)
    c: PointOnObject(g4,g-2)
    c: Coincident(g5,g4)
    c: Coincident(g5,g1)
    c: Parallel(g4,g5)
    c: Equal(g4,g5)
    c: DistanceX(g0,g0) = 5
    c: DistanceY(g1,g1) = 1
    c: DistanceY(g-3,g1) = 2
FEATURE [Part::Extrusion] Extrude023  label="Body Bottom Tab Rear Extrusion"
  Base = -> Sketch005025
  Dir = (0,-1,2e-16)
  DirMode = 2
  FaceMakerClass = Part::FaceMakerBullseye
  LengthFwd = 1
  LengthRev = 0
  Reversed = true
  Solid = true
  Symmetric = false
FEATURE [Part::MultiFuse] Fusion008  label="Body Bottom Tabs"
  Shapes = -> [Extrude024,Extrude023]
FEATURE [Part::Fillet] Fillet003  label="Body Bottom Tab Fillet"
  Base = -> Fusion008
  Edges = 8 edges r=0.4: [Edge4,Edge7,Edge10,Edge12,Edge16,Edge19,Edge22,Edge24]
FEATURE [Part::Cut] Cut014  label="Body Bottom Tab Cut"
  Base = -> Fusion004
  Tool = -> Fillet003
FEATURE [Drawing::FeaturePage] Page
  EditableTexts = Designed by Name | Date | Scale | Weight | Title | Subtitle | Drawing number | Sheet
  Template = <path>
FEATURE [TechDraw::DrawSVGTemplate] Template
  EditableTexts = Designed_by_Name=Designed by Name; Drawing_number=Drawing number; FC-Date=Date; FC-SC=Scale; FC-SH=Sheet; FC-Title=Title; Subtitle=Subtitle; Weight=Weight
  Height = 210
  Orientation = 1
  Width = 297
FEATURE [TechDraw::DrawPage] Page001
  KeepUpdated = true
  ProjectionType = 0
  Template = -> Template
FEATURE [TechDraw::DrawSVGTemplate] Template001
  EditableTexts = Approved1=Approved 1; Approved2=Approved 2; CheckedBy=Checked By; Code=Code; CompanyAddress=1234 Main St; CompanyName=Company Name; DrawingNumber=Drawing Number; DrawingTitle1=Drawing Title 1; DrawingTitle2=Drawing Title 2; DrawingTitle3=Drawing Title 3; DrawnBy=Drawn By; Revision=Rev; Scale=Scale; Sheet=Sheet n of m; Weight=Weight
  Height = 215.9
  Orientation = 1
  Width = 279.4
FEATURE [TechDraw::DrawProjGroupItem] ProjItem  label="Front"
  CoarseView = false
  Direction = (0,0,-1)
  Focus = 100
  HardHidden = false
  IsoCount = 0
  IsoHidden = false
  IsoVisible = false
  LockPosition = true
  Perspective = false
  Rotation = 0
  RotationVector = (1,0,0)
  ScaleType = 2
  SeamHidden = false
  SeamVisible = false
  SmoothHidden = false
  SmoothVisible = false
  Source = -> [Cut014]
  Type = 0
  X = 0
  Y = 0
FEATURE [TechDraw::DrawProjGroupItem] ProjItem001  label="Top"
  CoarseView = false
  Direction = (0,-1,0)
  Focus = 100
  HardHidden = false
  IsoCount = 0
  IsoHidden = false
  IsoVisible = false
  LockPosition = false
  Perspective = false
  Rotation = 0
  RotationVector = (1,0,0)
  ScaleType = 2
  SeamHidden = false
  SeamVisible = false
  SmoothHidden = false
  SmoothVisible = false
  Source = -> [Cut014]
  Type = 4
  X = 0
  Y = -80
FEATURE [TechDraw::DrawViewDimension] Dimension
  Arbitrary = false
  FormatSpec = ⌀%.2f
  LockPosition = false
  MeasureType = 1
  OverTolerance = 0
  References2D = -> [ProjItem]
  Rotation = 0
  ScaleType = 0
  Type = 5
  UnderTolerance = 0
  X = 23.8806
  Y = 42.8876
FEATURE [TechDraw::DrawViewDimension] Dimension001
  Arbitrary = false
  FormatSpec = %.2f
  LockPosition = false
  MeasureType = 1
  OverTolerance = 0
  Rotation = 0
  ScaleType = 0
  Type = 1
  UnderTolerance = 0
  X = 6.82303
  Y = 21.823
FEATURE [TechDraw::DrawViewDimension] Dimension002
  Arbitrary = false
  FormatSpec = %.2f
  LockPosition = false
  MeasureType = 1
  OverTolerance = 0
  Rotation = 0
  ScaleType = 0
  Type = 2
  UnderTolerance = 0
  X = -28.7612
  Y = -5.86095
FEATURE [TechDraw::DrawViewDimension] Dimension003
  Arbitrary = false
  FormatSpec = ⌀%.2f
  LockPosition = false
  MeasureType = 1
  OverTolerance = 0
  References2D = -> [ProjItem]
  Rotation = 0
  ScaleType = 0
  Type = 5
  UnderTolerance = 0
  X = -15.2332
  Y = 23.1717
FEATURE [TechDraw::DrawViewSection] Section  label="Section A - A"
  BaseView = -> ProjItem
  CoarseView = false
  Direction = (0,-1,1e-16)
  Focus = 100
  FuseBeforeCut = true
  HardHidden = false
  HatchScale = 1
  IsoCount = 0
  IsoHidden = false
  IsoVisible = false
  LockPosition = false
  NameGeomPattern = Diamond
  Perspective = false
  Rotation = 0
  ScaleType = 2
  SeamHidden = false
  SeamVisible = false
  SectionDirection = 2
  SectionNormal = (0,-1,1e-16)
  SectionOrigin = (5.1e-15,-2.5,32)
  SectionSymbol = A
  SmoothHidden = false
  SmoothVisible = false
  Source = -> [Cut014]
  X = 162.606
  Y = 151.325
FEATURE [TechDraw::DrawProjGroupItem] ProjItem002  label="Bottom"
  CoarseView = false
  Direction = (0,1,0)
  Focus = 100
  HardHidden = false
  IsoCount = 0
  IsoHidden = false
  IsoVisible = false
  LockPosition = false
  Perspective = false
  Rotation = 0
  RotationVector = (1,0,0)
  ScaleType = 2
  SeamHidden = false
  SeamVisible = false
  SmoothHidden = false
  SmoothVisible = false
  Source = -> [Cut014]
  Type = 5
  X = 0
  Y = 80
FEATURE [TechDraw::DrawProjGroup] ProjGroup
  Anchor = -> ProjItem
  AutoDistribute = true
  LockPosition = false
  ProjectionType = 0
  Rotation = 0
  ScaleType = 0
  Source = -> [Cut014]
  Views = -> [ProjItem,ProjItem001,ProjItem002]
  X = 70.0077
  Y = 147.913
  spacingX = 15
  spacingY = 15
FEATURE [TechDraw::DrawPage] Page002
  KeepUpdated = true
  ProjectionType = 0
  Template = -> Template001
  Views = -> [ProjGroup,Dimension,Dimension001,Dimension002,Dimension003,Section]
FEATURE [TechDraw::DrawSVGTemplate] Template002
  EditableTexts = Code=Code; DrawingNumber=v0.1.0; DrawingTitle1=MessageBox; DrawnBy=Desone Burns II; Scale=1:1; Sheet=Sheet 1 of 1
  Height = 215.9
  Orientation = 1
  Width = 279.4
FEATURE [TechDraw::DrawProjGroupItem] ProjItem004  label="LCD Mount"
  CoarseView = false
  Direction = (0,0,-1)
  Focus = 100
  HardHidden = false
  IsoCount = 0
  IsoHidden = false
  IsoVisible = false
  LockPosition = false
  Perspective = false
  Rotation = 0
  RotationVector = (1,0,0)
  ScaleType = 2
  SeamHidden = false
  SeamVisible = false
  SmoothHidden = false
  SmoothVisible = false
  Source = -> [Cut014]
  Type = 5
  X = 0
  Y = 80
FEATURE [TechDraw::DrawProjGroup] ProjGroup001
  AutoDistribute = true
  LockPosition = false
  ProjectionType = 0
  Rotation = 0
  ScaleType = 0
  Source = -> [Cut014]
  Views = -> [ProjItem004]
  X = 68.5456
  Y = 62.1383
  spacingX = 15
  spacingY = 15
FEATURE [TechDraw::DrawViewSection] Section001  label="MCU Mount"
  BaseView = -> ProjItem004
  CoarseView = false
  Direction = (1,0,0)
  Focus = 100
  FuseBeforeCut = true
  HardHidden = false
  HatchScale = 1
  IsoCount = 0
  IsoHidden = false
  IsoVisible = false
  LockPosition = false
  NameGeomPattern = Diamond
  Perspective = false
  Rotation = 0
  ScaleType = 2
  SeamHidden = false
  SeamVisible = false
  SectionDirection = 1
  SectionNormal = (1,0,0)
  SectionOrigin = (3.6e-15,-0.5,32)
  SectionSymbol = A
  SmoothHidden = false
  SmoothVisible = false
  Source = -> [Cut014]
  X = 63.867
  Y = 56.8238
FEATURE [TechDraw::DrawViewDimension] Dimension004
  Arbitrary = false
  FormatSpec = %.2f
  LockPosition = false
  MeasureType = 1
  OverTolerance = 0
  References2D = -> [ProjItem004]
  Rotation = 0
  ScaleType = 0
  Type = 2
  UnderTolerance = 0
  X = -41.0808
  Y = 0.440121
FEATURE [Sketcher::SketchObject] Sketch005029  label="Symbol Guard Interior"
  MapMode = 5
  Placement = pos=(0,-30,0) rot=(0,0.707107,0.707107;3.14159rad)
  Support = -> [ShapeBinder]
  sketch-geometry (2):
    g0: Circle CenterX=0 CenterY=30 CenterZ=0 NormalX=0 NormalY=0 NormalZ=1 AngleXU=0 Radius=19
    g1: LineSegment [constr] StartX=0 StartY=30 StartZ=0 EndX=0 EndY=0 EndZ=0
  constraints (5):
    c: PointOnObject(g0,g-2)
    c: Coincident(g1,g0)
    c: Coincident(g1,g-1)
    c: DistanceY(g1,g1) = 30
    c: Radius(g0) = 19
FEATURE [Sketcher::SketchObject] Sketch005030  label="Symbol Guard Exterior"
  MapMode = 5
  Placement = pos=(0,-30,0) rot=(0,0.707107,0.707107;3.14159rad)
  Support = -> [ShapeBinder]
  sketch-geometry (2):
    g0: LineSegment [constr] StartX=0 StartY=0 StartZ=0 EndX=0 EndY=30 EndZ=0
    g1: Circle CenterX=0 CenterY=30 CenterZ=0 NormalX=0 NormalY=0 NormalZ=1 AngleXU=0 Radius=21
  constraints (5):
    c: Coincident(g0,g-1)
    c: PointOnObject(g0,g-2)
    c: DistanceY(g0,g0) = 30
    c: Coincident(g1,g0)
    c: Radius(g1) = 21
FEATURE [PartDesign::Body] Body
  Group = -> [Sketch,CopyExtrude,Sketch001,Sketch002,CopyCut001,Sketch003,Sketch004,DatumLine,CopyCut003,CopyCut003001,DatumPlane,CopyCut003002,CopyCut003003,ShapeBinder,Sketch005011,Sketch005012,Sketch005013,Sketch005017,ShapeBinder008,ShapeBinder009,ShapeBinder010,Sketch005025,Sketch005026,CopyCut002,Sketch005027,Sketch005028,Sketch005029,Sketch005030]
  Origin = -> Origin
FEATURE [Part::Extrusion] Extrude027
  Base = -> Sketch005030
  Dir = (0,1,-2e-16)
  DirMode = 2
  FaceMakerClass = Part::FaceMakerBullseye
  LengthFwd = 3
  LengthRev = 0
  Solid = true
  Symmetric = false
FEATURE [Part::Extrusion] Extrude028
  Base = -> Sketch005029
  Dir = (0,1,-2e-16)
  DirMode = 2
  FaceMakerClass = Part::FaceMakerBullseye
  LengthFwd = 3
  LengthRev = 0
  Solid = true
  Symmetric = false
FEATURE [Part::Cut] Cut015  label="Symbol Guard"
  Base = -> Extrude027
  Tool = -> Extrude028
FEATURE [Part::MultiFuse] Fusion  label="Symbol Guard Fusion"
  Shapes = -> [Cut015,Cut014]
FEATURE [TechDraw::DrawViewPart] View
  CoarseView = false
  Direction = (0,1,0)
  Focus = 100
  HardHidden = false
  IsoCount = 0
  IsoHidden = false
  IsoVisible = false
  LockPosition = false
  Perspective = false
  Rotation = 0
  ScaleType = 0
  SeamHidden = false
  SeamVisible = false
  SmoothHidden = false
  SmoothVisible = false
  Source = -> [Fusion]
  X = 139.7
  Y = 107.95
FEATURE [TechDraw::DrawPage] Page003
  KeepUpdated = true
  ProjectionType = 0
  Template = -> Template002
  Views = -> [ProjGroup001,Section001,Dimension004,View]
note: 1 file-system path scrubbed to <path> (originals preserved in the JSON sidecar)
